# Revit family: 0044631
name_source: partatom
category: Lighting Fixtures
units: mm (PartAtom-declared; Revit-internal decimal feet)

## family parameters
Cut with Voids When Loaded = No
Host = Face
Light Source = Yes
Maintain Annotation Orientation = No
OmniClass Number = 23.80.70.00
OmniClass Title = Lighting
Part Type = Normal
Room Calculation Point = No
Round Connector Dimension = Use Diameter
Shared = No

## types (1)
- START PANEL UGR19 1200X300 DALI 3800 840
    Apparent Load = 32 VA
    Assembly Code = D5020200
    AssetType = Fixed
    ClassificationName = Uniclass2015
    ClassificationValue = EF_70_80
    Color Filter = 16777215
    Cost = 0 $
    Default Elevation = 1219 mm
    Description = LED Panel with backlit technology, ideal for general indoor lighting applications such as breakout areas, offices and meeting rooms. Extruded aluminium frame, passive cooling. Low glaring UGR<19. RG0, 90 degree beam angle , optical system: PS diffuser with Prismatic finish. Light color temperature: 4000K Neutral White, total system power: 29W , total fixture output: 3800lm, efficacy: 131 lm/W, Ra80 typical, LED chromacity: 3 step MacAdam ellipse (SDCM3), lifespan: 100,000 hours at 70% of the original output (L70B50), IR/UV free light source without heat radiation, operating voltage: 220-240V / 50-60Hz, low flicker, DALI dimmable driver, electrical protection: Class II. Degree of Protection: IP40/IP20, suitable for indoor environment only. Nominal size: 1195x295mm, Loop in / loop out wiring, saftey cables & quick connector included, 26mm nominal height, White color frame, weight: 1,97Kg.
    Dimming Lamp Color Temperature Shift = <None>
    DimmingControlOptions = DALI-2
    DocumentationLiterature = https://www.sylvania-lighting.com code/0044631/
    ElectricShockClassification = Class II
    EmergencyLight = No
    Emit Shape Visible in Rendering = No
    Emit from Rectangle Length = 1163 mm  [stored 3.81562 ft]
    Emit from Rectangle Width = 264 mm  [stored 0.866142 ft]
    Export Type to IFC As = IfcLightFixtureType
    IfcExportAs = IfcLightFixtureType
    IfcExportType = IfcLightFixtureType
    ImpactProtectionIndex = IK03
    IngressProtection = IP40/20
    InputNominalFrequency = 50/60Hz
    InputVoltage = 220-240 V
    Keynote = 16500
    Lamp = LED
    LampColourRenderingIndex = 80
    LampColourTemperature = 4000 K
    LampMacAdamStep = 3
    LampNominalLuminous = 3800
    LampsType = LED
    LuminaireType = Ceiling recessed mounting,Suspended
    LuminousEfficacy = 131 lm/W
    Manufacturer = Feilo Sylvania
    ManufacturerName = Feilo Sylvania
    Material = Steel
    Material_1_SYL = Steel_RAL9003_White
    Material_2_SYL = Polystyrene_4000K
    Material_3_SYL = <By Category>
    Material_4_SYL = <By Category>
    Model = START PANEL UGR19 1200X300 DALI 3800 840
    ModelNumber = 0044631
    ModelReference = START PANEL UGR19 1200X300 DALI 3800 840
    Name = START PANEL UGR19 1200X300 DALI 3800 840
    NominalDepth = 295 mm  [stored 0.967848 ft]
    NominalHeight = 26 mm
    NominalLength = 1195 mm  [stored 3.9206 ft]
    Photometric Web File = 0044631.IES
    PowerConsumption = 29 W
    PowerFactor = 0.9
    Tilt Angle = -90.00°
    Type IFC Predefined Type = IfcLightFixtureType
    Type Image = <None>
    TypeName = START Panel IP40 UGR19 1200x300
    URL = http://www.sylvania-group.com
    Voltage = 230 V
    WarrantyDescription = http://www.sylvania-group.com
    WarrantyDurationParts = 5
    WarrantyDurationUnit = Years
    Weight = 1.971

note: [stored X ft] marks values corroborated as IEEE doubles in the binary element streams (Revit-internal decimal feet)

## geometry (parser evidence)
native form markers: Sweep x2
no freeform markers — native parametric forms only
